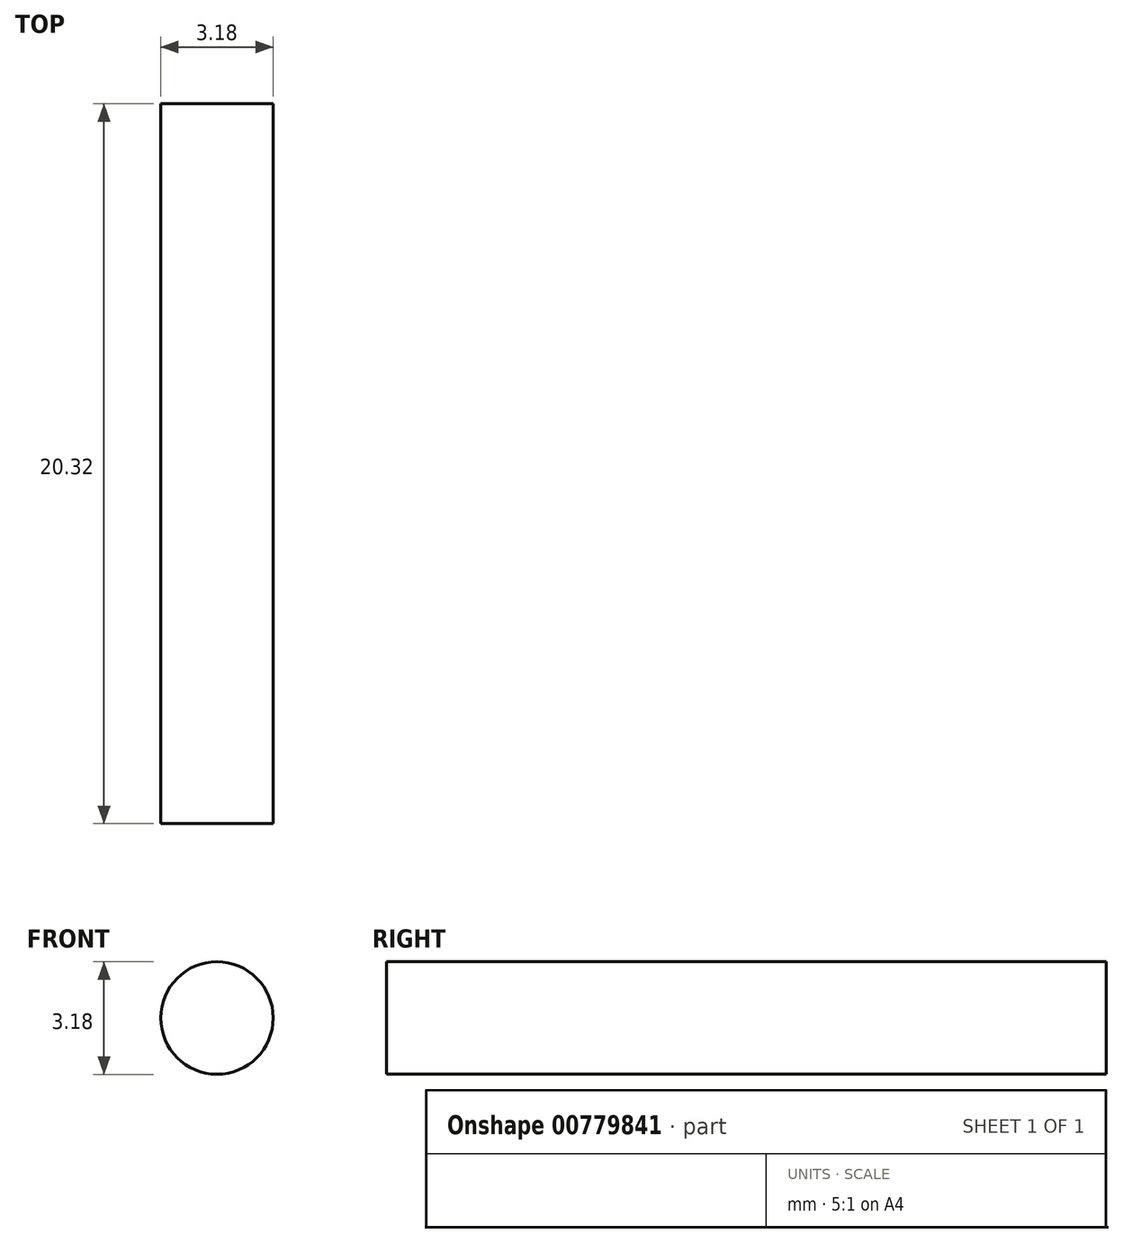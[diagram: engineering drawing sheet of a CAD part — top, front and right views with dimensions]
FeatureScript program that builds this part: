
annotation { "Feature Type Name" : "Feature", "Feature Type Description" : "" }
export const myFeature = defineFeature(function(context is Context, id is Id, definition is map)
    precondition{}
    {
        {
            var Q0;
            Q0=qCreatedBy(makeId("Front.planeOp"),FACE);
            var sketch = newSketch(context, id + "F0", { "sketchPlane" : qUnion([Q0])});
            skCircle(sketch, "E0", {"center": v(-39.85, 35.27) * mm, "radius": 1.59 * mm});
            skSolve(sketch);
        }
        {
            var Q0;
            Q0=makeQuery(id+"F0.imprint","IMPRINT",FACE,{"disambiguationData":[TD([[makeQuery(id+"F0.imprint","IMPRINT",EDGE,{"derivedFrom":sQuery(id+"F0.wireOp",EDGE,"E0")}),1.0]])]});
            extrude(context, id + "F1", {"entities" : qUnion([Q0]), "depth" : 20.32 * mm, "offsetDistance" : 25.4 * mm});
        }
    });
